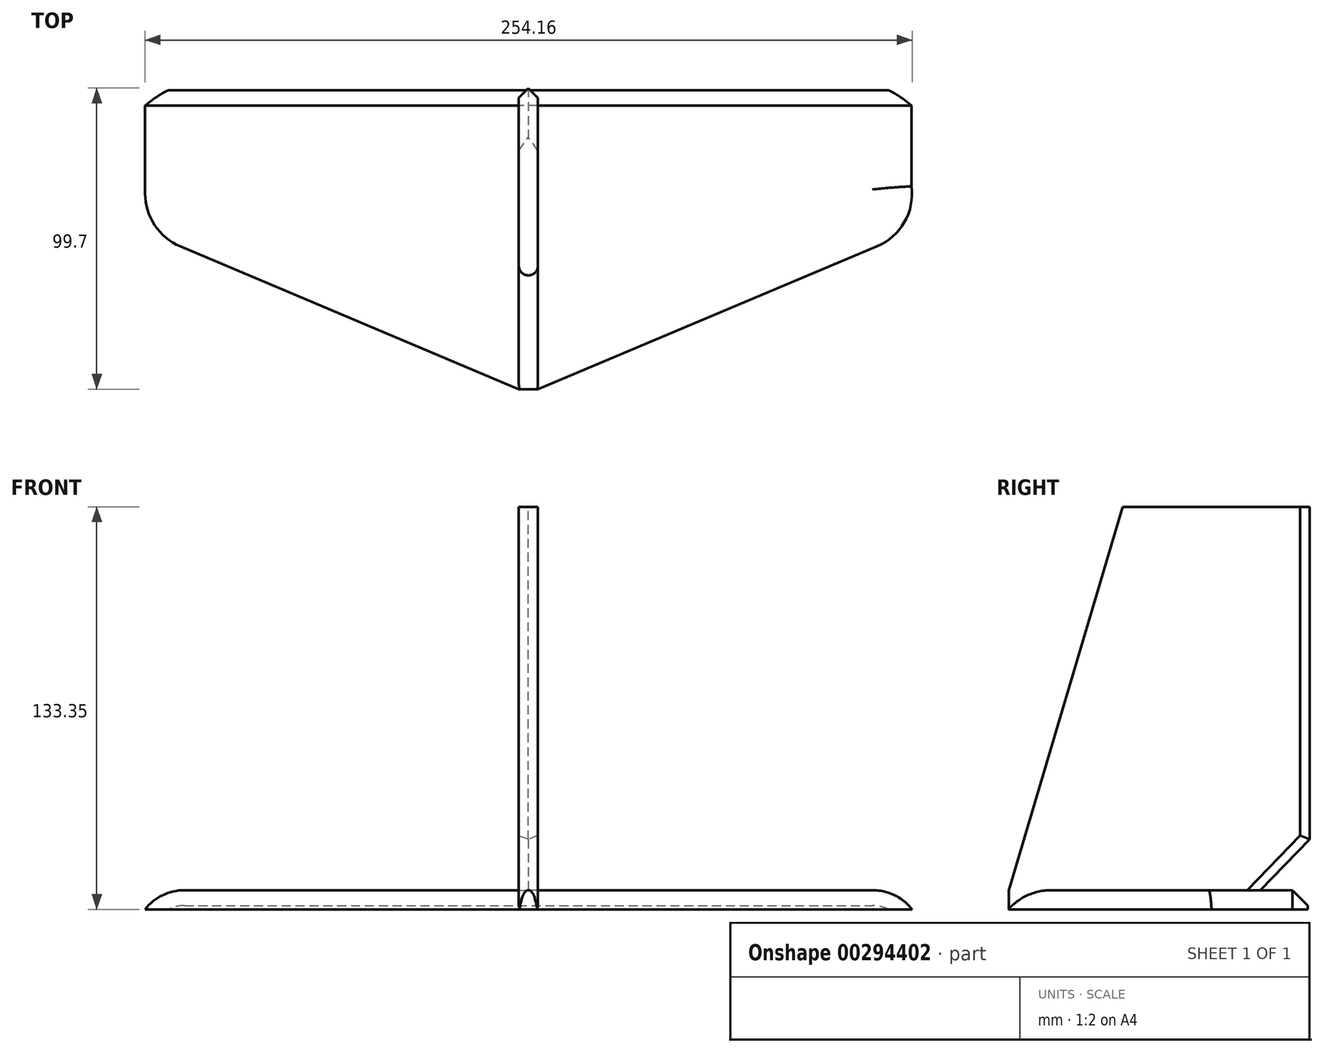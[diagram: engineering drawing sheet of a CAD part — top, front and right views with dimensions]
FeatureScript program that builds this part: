
annotation { "Feature Type Name" : "Feature", "Feature Type Description" : "" }
export const myFeature = defineFeature(function(context is Context, id is Id, definition is map)
    precondition{}
    {
        {
            var Q0;
            Q0=qCreatedBy(makeId("Right.planeOp"),FACE);
            var sketch = newSketch(context, id + "F0", { "sketchPlane" : qUnion([Q0])});
            skLineSegment(sketch, "E0.bottom", {"start": v(0, 60.83) * mm, "end": v(63.9, 60.83) * mm});
            skLineSegment(sketch, "E0.top", {"start": v(-37.7, -66.17) * mm, "end": v(48.36, -66.17) * mm});
            skLineSegment(sketch, "E0.right", {"start": v(63.9, 60.83) * mm, "end": v(63.9, -50.16) * mm});
            skLineSegment(sketch, "E1", {"start": v(-37.7, -66.17) * mm, "end": v(0, 60.83) * mm});
            skLineSegment(sketch, "E2", {"start": v(63.9, -50.16) * mm, "end": v(48.36, -66.17) * mm});
            skSolve(sketch);
        }
        {
            var Q0;
            Q0=makeQuery(id+"F0.imprint","IMPRINT",FACE,{"disambiguationData":[TD([[makeQuery(id+"F0.imprint","IMPRINT",EDGE,{"derivedFrom":sQuery(id+"F0.wireOp",EDGE,"E0.bottom")}),-1.0]])]});
            extrude(context, id + "F1", {"entities" : qUnion([Q0]), "depth" : 6.35 * mm, "offsetDistance" : 25.4 * mm});
        }
        {
            var Q0;
            Q0=makeQuery(id+"F1.opExtrude","SWEPT_FACE",FACE,{"disambiguationData":[OSD([sQuery(id+"F0.wireOp",EDGE,"E0.top")])]});
            var sketch = newSketch(context, id + "F2", { "sketchPlane" : qUnion([Q0])});
            skLineSegment(sketch, "E3.bottom", {"start": v(0, 37.7) * mm, "end": v(6.35, 37.7) * mm});
            skLineSegment(sketch, "E3.top", {"start": v(-123.83, -61.35) * mm, "end": v(130.17, -61.35) * mm});
            skLineSegment(sketch, "E3.left", {"start": v(-123.83, -27.1) * mm, "end": v(-123.83, -61.35) * mm});
            skLineSegment(sketch, "E3.right", {"start": v(130.17, -24.7) * mm, "end": v(130.17, -61.35) * mm});
            skCircle(sketch, "E4", {"center": v(-104.78, -27.1) * mm, "radius": 19.05 * mm});
            skCircle(sketch, "E5", {"center": v(111.28, -27.1) * mm, "radius": 19.05 * mm});
            skLineSegment(sketch, "E6", {"start": v(0, 37.7) * mm, "end": v(-112.17, -9.54) * mm});
            skLineSegment(sketch, "E7", {"start": v(6.35, 37.7) * mm, "end": v(118.66, -9.54) * mm});
            skPoint(sketch, "E8.orphan", {"position": v(-123.83, 37.7) * mm});
            skSolve(sketch);
        }
        {
            var Q0;
            Q0=qSketchRegion(id+"F2",true);
            extrude(context, id + "F3", {"entities" : qUnion([Q0]), "operationType" : NewBodyOperationType.ADD, "depth" : 6.35 * mm, "offsetDistance" : 25.4 * mm});
        }
        {
            var Q0;
            Q0=makeQuery(id+"F1.opExtrude","CAP_EDGE",EDGE,{"disambiguationData":[OSD([sQuery(id+"F0.wireOp",EDGE,"E1")])],"isStart":false});
            var Q1;
            Q1=makeQuery(id+"F1.opExtrude","CAP_EDGE",EDGE,{"disambiguationData":[OSD([sQuery(id+"F0.wireOp",EDGE,"E1")])],"isStart":true});
            fillet(context, id + "F4", {"entities" : qUnion([Q0, Q1]), "radius" : 3.07 * mm, "tangentPropagation" : true, "allowEdgeOverflow" : false});
        }
        {
            var Q0;
            Q0=makeQuery(id+"F3.opExtrude","CAP_EDGE",EDGE,{"disambiguationData":[OSD([sQuery(id+"F2.wireOp",EDGE,"E7")])],"isStart":true});
            var Q1;
            Q1=makeQuery(id+"F3.opExtrude","CAP_EDGE",EDGE,{"disambiguationData":[OSD([sQuery(id+"F2.wireOp",EDGE,"E6")])],"isStart":true});
            var Q2;
            Q2=makeQuery(id+"F3.opExtrude","CAP_EDGE",EDGE,{"disambiguationData":[OSD([sQuery(id+"F2.wireOp",EDGE,"E5")])],"isStart":true});
            var Q3;
            Q3=makeQuery(id+"F3.opExtrude","CAP_EDGE",EDGE,{"disambiguationData":[OSD([sQuery(id+"F2.wireOp",EDGE,"E3.right")])],"isStart":true});
            fillet(context, id + "F5", {"entities" : qUnion([Q0, Q1, Q2, Q3]), "radius" : 16.56 * mm, "tangentPropagation" : true, "allowEdgeOverflow" : false});
        }
        {
            var Q0;
            Q0=makeQuery(id+"F1.opExtrude","CAP_EDGE",EDGE,{"disambiguationData":[OSD([sQuery(id+"F0.wireOp",EDGE,"E0.right")])],"isStart":true});
            var Q1;
            Q1=makeQuery(id+"F1.opExtrude","CAP_EDGE",EDGE,{"disambiguationData":[OSD([sQuery(id+"F0.wireOp",EDGE,"E0.right")])],"isStart":false});
            chamfer(context, id + "F6", {"entities" : qUnion([Q0, Q1]), "width" : 5.08 * mm, "tangentPropagation" : true});
        }
        {
            var Q0;
            Q0=makeQuery(id+"F1.opExtrude","CAP_EDGE",EDGE,{"disambiguationData":[OSD([sQuery(id+"F0.wireOp",EDGE,"E2")])],"isStart":false});
            var Q1;
            Q1=makeQuery(id+"F1.opExtrude","CAP_EDGE",EDGE,{"disambiguationData":[OSD([sQuery(id+"F0.wireOp",EDGE,"E2")])],"isStart":true});
            chamfer(context, id + "F7", {"entities" : qUnion([Q0, Q1]), "width" : 5.08 * mm, "tangentPropagation" : true});
        }
        {
            var Q0;
            Q0=makeQuery(id+"F3.opExtrude","CAP_EDGE",EDGE,{"disambiguationData":[OSD([sQuery(id+"F2.wireOp",EDGE,"E3.top")])],"isStart":true});
            chamfer(context, id + "F8", {"entities" : qUnion([Q0]), "width" : 5.08 * mm, "tangentPropagation" : true});
        }
    });
